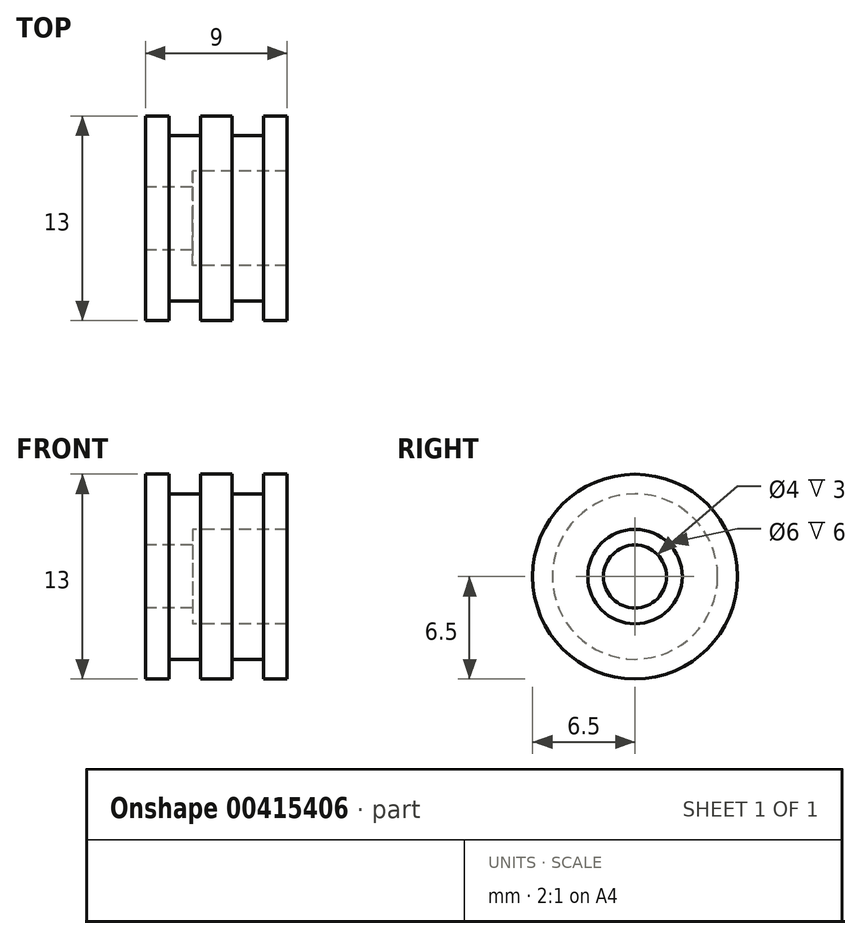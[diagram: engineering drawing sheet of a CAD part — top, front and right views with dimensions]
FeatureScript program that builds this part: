
annotation { "Feature Type Name" : "Feature", "Feature Type Description" : "" }
export const myFeature = defineFeature(function(context is Context, id is Id, definition is map)
    precondition{}
    {
        {
            var Q0;
            Q0=qCreatedBy(makeId("Top.planeOp"),FACE);
            var sketch = newSketch(context, id + "F0", { "sketchPlane" : qUnion([Q0])});
            skLineSegment(sketch, "E0", {"start": v(0, 2) * mm, "end": v(0, 6.5) * mm});
            skLineSegment(sketch, "E1", {"start": v(0, 6.5) * mm, "end": v(1.5, 6.5) * mm});
            skLineSegment(sketch, "E2", {"start": v(1.5, 6.5) * mm, "end": v(1.5, 5.25) * mm});
            skLineSegment(sketch, "E3", {"start": v(1.5, 5.25) * mm, "end": v(3.5, 5.25) * mm});
            skLineSegment(sketch, "E4", {"start": v(3.5, 5.25) * mm, "end": v(3.5, 6.5) * mm});
            skLineSegment(sketch, "E5", {"start": v(3.5, 6.5) * mm, "end": v(5.5, 6.5) * mm});
            skLineSegment(sketch, "E6", {"start": v(5.5, 6.5) * mm, "end": v(5.5, 5.25) * mm});
            skLineSegment(sketch, "E7", {"start": v(5.5, 5.25) * mm, "end": v(7.5, 5.25) * mm});
            skLineSegment(sketch, "E8", {"start": v(7.5, 5.25) * mm, "end": v(7.5, 6.5) * mm});
            skLineSegment(sketch, "E9", {"start": v(7.5, 6.5) * mm, "end": v(9, 6.5) * mm});
            skLineSegment(sketch, "E10", {"start": v(9, 6.5) * mm, "end": v(9, 4.79) * mm});
            skLineSegment(sketch, "E11", {"start": v(9, 4.79) * mm, "end": v(9, 4.79) * mm});
            skLineSegment(sketch, "E12", {"start": v(9, 4.79) * mm, "end": v(9, 3) * mm});
            skLineSegment(sketch, "E13", {"start": v(9, 3) * mm, "end": v(3, 3) * mm});
            skLineSegment(sketch, "E14", {"start": v(3, 3) * mm, "end": v(3, 2) * mm});
            skLineSegment(sketch, "E15", {"start": v(3, 2) * mm, "end": v(0, 2) * mm});
            skLineSegment(sketch, "E16", {"start": v(0, 0) * mm, "end": v(7.56, 0) * mm, "construction": true});
            skSolve(sketch);
        }
        {
            var Q0;
            Q0=makeQuery(id+"F0.imprint","IMPRINT",FACE,{"disambiguationData":[TD([[makeQuery(id+"F0.imprint","IMPRINT",EDGE,{"derivedFrom":sQuery(id+"F0.wireOp",EDGE,"E0")}),-1.0]])]});
            var Q1;
            Q1=sQuery(id+"F0.wireOp",EDGE,"E16");
            revolve(context, id + "F1", {"surfaceOperationType" : NewSurfaceOperationType.NEW, "entities" : qUnion([Q0]), "axis" : qUnion([Q1]), "revolveType" : RevolveType.FULL});
        }
    });
